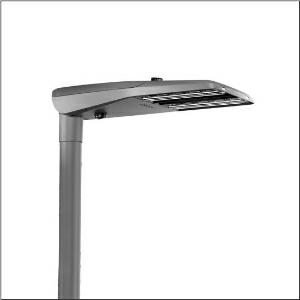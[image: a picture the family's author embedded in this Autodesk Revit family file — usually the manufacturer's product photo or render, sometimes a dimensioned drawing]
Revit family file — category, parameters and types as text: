
# Revit family: streetlight_sl_11_iq_midi___pc-l_5xc3e51y08me_36d5
name_source: partatom
category: Lighting Fixtures
units: mm (PartAtom-declared; Revit-internal decimal feet)

## family parameters
Cut with Voids When Loaded = No
Host = Face
Light Source = No
Part Type = Normal
Room Calculation Point = No
Round Connector Dimension = Use Diameter
Shared = No

## types (1)
- --- (1 x LED, 15540 lm, 122.7 W, 3000K)
    Apparent Load = 123 VA
    CIE Flux Codes = 37 73 96 100 100
    Color Rendering = 70
    Color Temperature = 3000K
    Default Elevation = 1800 mm
    Description = Streetlight SL 11 iQ midi, mast luminaire, primary light control with 3 zone facetted reflector, of plastic, silver coated, highly specular, primary optical cover: cover, of PMMA, transparent, light distribution: PC-L, light emission: direct distribution, primary light characteristic: asymmetric, left, installation type: post-top, side-entry, LED, High Power LED, rated luminous flux: 15.540lm, luminous efficacy: 126lm/W, light colour: 730, colour temperature: 3000K, control: presetting dimming logarithmic, Street-Remote, Auto-Match, Temp-Guard, Lumen-Switch, Night-Set, Smart-Wire, Light-Fading, Desk-Remote (wireless, voltage-free reading and setting of iQ features in the workshop via application-optimized NFC function/RFID function), optimised constant luminous flux control (CLO 2.0), with cable H07RN-F 5x 1.5mm², mains connection: 220..240V, AC, 50/60Hz, connection cable pre-assembled, cable length: 12,5m, start of lifetime: 123W, end of service life: 130W, reduction: 56W, luminaire housing, of diecast aluminium, powder-coated, Siteco® metallic grey (DB 702S), please order mast flange separately, inclination adjustable without tools: 0°, 5°, 10°, 15° (post-top) | 0°, -5°, -10°, -15° (side-entry), sealing non-destructively replaceable, multi-level sealing system, length: 780mm, width: 376mm, height: 118mm, spigot size: 60/76mm (post-top) and 42/60/76mm (side-entry), mast flange for spigot size: 42mm: 5XC10008XM4, 60mm: 5XC10008XM2, 76/60mm: 5XC10108XM1, equipment: Power, Smart Interface below and above, protection rating (complete): IP66, insulation class (complete): insulation class II (safety insulation), certification: CE, ENEC in preparation, impact resistance: IK09, permissible operating ambient temperature for outdoor applications: -25..+50°C, standard-compliant lighting for roads and squares, packaging unit: 1 piece

Light Distribution: PC-L
    Height = 118 mm
    Lamp = 1 x LED
    Lamp Light Flux = 15540 lm
    Lamp Power = 122.7 W
    Lamp count = 1
    Length = 780 mm
    Luminous efficacy = 127 lm/W
    Manufacturer = Siteco
    ModVariant = No
    Model = 5XC3E51Y08ME
    Number of Poles = 1
    OnlyDefault = Yes
    Power Factor = 1
    Product Name = Streetlight SL 11 iQ midi | PC-L
    Product group = mast luminaire | pylon top
    ProductGroupID = 6100
    Protection Class = Protection class II
    Protection Degree = IP 66
    RLX_Detail_Level = 1
    RlxData = <blob elided: 73509 chars, md5=8b897cd9>
    Socket = socket
    Standby Power = 0 W
    System Light Flux = 15540 lm
    System Power = 123 W
    Type Comments = factory setting: luminous flux: 100 % | dim-lin: 254 | 552 mA
    Type Image = l_1004429.jpg
    URL = http://relux.com
    VarID = @adj_043391
    Voltage = 0 V
    Weight = 0.00 kg
    Width = 376 mm

## geometry (parser evidence)
native form markers: Blend x4, Sweep x11
no freeform markers — native parametric forms only
